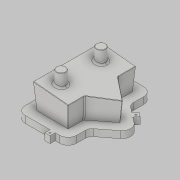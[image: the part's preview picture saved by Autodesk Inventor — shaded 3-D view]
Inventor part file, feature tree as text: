
AUTODESK INVENTOR PART (.ipt)
format: ipt  version: 2019 (Build 230136000, 136)  size: 386,560 bytes
history: native  units: mm
features: extrude x5, sketch x4, draft x1, fillet x1, shell x1, boolean_combine x1, delete_face x1, projected_geometry x1
ambient origin geometry x8: Origin, YZ Plane, XZ Plane, XY Plane, X Axis, Y Axis, Z Axis, Center Point
bodies: Solid1 (feature_tree), Solid2 (feature_tree)
feature tree (15):
  extrude  "Extrusion1"  Depth=200.0mm
  extrude  "Extrusion2"  Depth=42.0mm
  extrude  "Extrusion3"  TaperAngle=75.0deg  [1 undecoded]
  draft  "FaceDraft1"
  fillet  "Fillet1"  Radius=52.0mm
  shell  "Shell2"  Thickness=110.0mm
  extrude  "Extrusion4"  Depth=77.0mm
  boolean_combine  "Combine1"
  delete_face  "Delete Face1"
  extrude  "Extrusion7"  Depth=110.0mm TaperAngle=0.0deg
  sketch  "Sketch1"  dims[d0=100.0mm d1=200.0mm]
  sketch  "Sketch2"  dims[d2=35.0mm d4=42.0mm]
  sketch  "Sketch3"  dims[d5=42.0mm d6=75.0deg d7=52.0mm d8=110.0mm d9=0.0mm]
  sketch  "Sketch6"  dims[d11=62.0mm d12=77.0mm d13=110.0mm d14=0.0mm d22=110.0mm d23=0.0mm d25=0.698132mm d26=5.0mm d27=1.0mm d28=4.0mm d29=20.000002mm d30=20.0mm d31=20.0mm d32=130.0mm d33=0.0mm d34=15.0mm d35=30.0mm d36=30.0mm d37=15.0mm d38=15.0mm d39=30.0mm d40=20.0mm d41=40.0mm d42=5.0mm d43=7.5mm d44=5.0mm d45=7.5mm d46=7.5mm d47=5.0mm d48=7.5mm d49=7.5mm d59=20.0mm d60=0.0mm]
  projected_geometry  "Projected Loop1"
note: 1 required parameter value undecoded (feature->parameter linkage not recoverable at this tier; creation-order binding heuristic only, values carry confidence <= 0.55)
